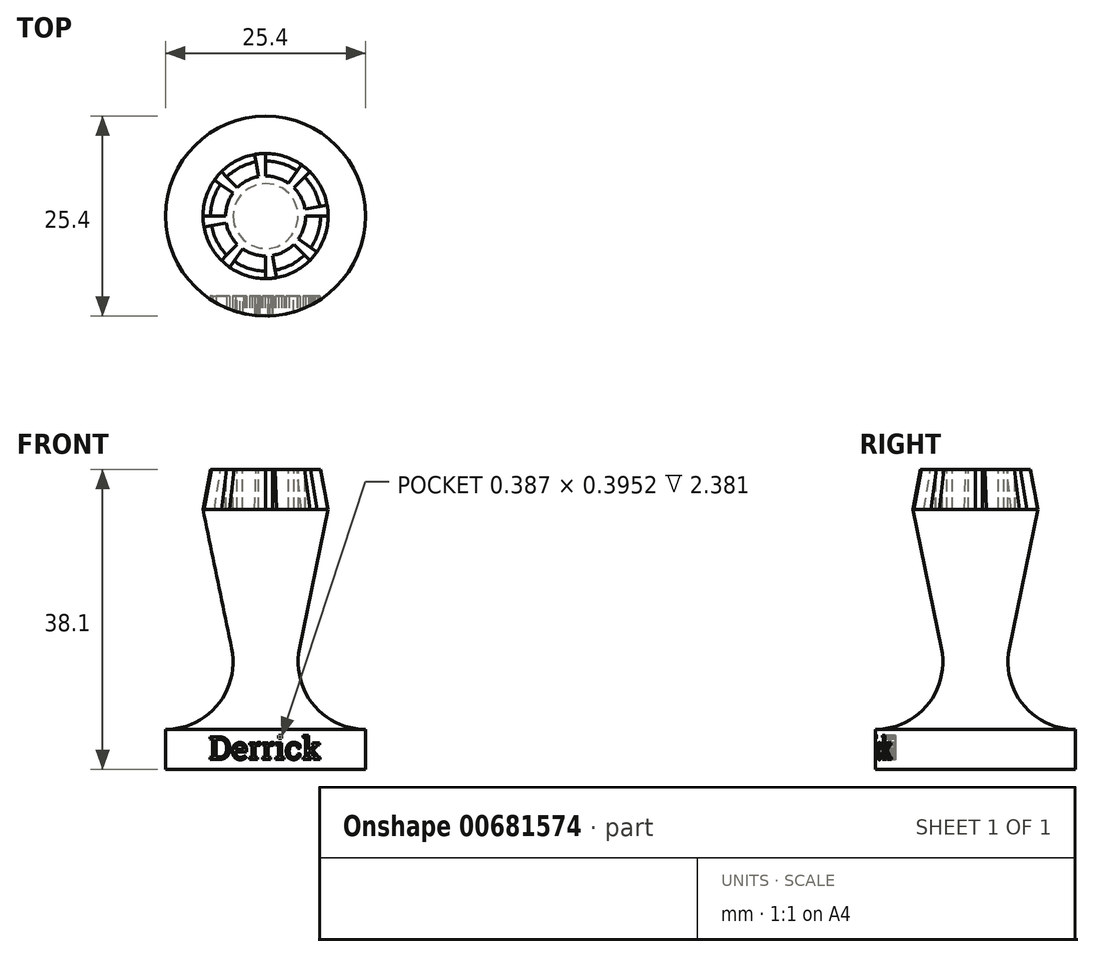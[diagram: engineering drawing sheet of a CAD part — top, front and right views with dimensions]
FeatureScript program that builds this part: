
annotation { "Feature Type Name" : "Feature", "Feature Type Description" : "" }
export const myFeature = defineFeature(function(context is Context, id is Id, definition is map)
    precondition{}
    {
        {
            var Q0;
            Q0=qCreatedBy(makeId("Front.planeOp"),FACE);
            var sketch = newSketch(context, id + "F0", { "sketchPlane" : qUnion([Q0])});
            skLineSegment(sketch, "E0", {"start": v(0, 0) * mm, "end": v(12.7, 0) * mm});
            skLineSegment(sketch, "E1", {"start": v(12.7, 0) * mm, "end": v(12.7, 5.08) * mm});
            skLineSegment(sketch, "E2", {"start": v(0, 0) * mm, "end": v(0, 38.1) * mm});
            skLineSegment(sketch, "E3", {"start": v(0, 38.1) * mm, "end": v(6.99, 38.1) * mm});
            skLineSegment(sketch, "E4", {"start": v(0, 33.02) * mm, "end": v(7.95, 33.02) * mm, "construction": true});
            skLineSegment(sketch, "E5", {"start": v(7.95, 33.02) * mm, "end": v(6.99, 38.1) * mm});
            skArc(sketch, "E6", {"start": v(4.32, 15.36) * mm, "mid": v(6.07, 8.23) * mm, "end": v(12.7, 5.08) * mm});
            skLineSegment(sketch, "E7", {"start": v(7.95, 33.02) * mm, "end": v(4.32, 15.36) * mm});
            skSolve(sketch);
        }
        {
            var Q0;
            Q0=makeQuery(id+"F0.imprint","IMPRINT",FACE,{"disambiguationData":[TD([[makeQuery(id+"F0.imprint","IMPRINT",EDGE,{"derivedFrom":sQuery(id+"F0.wireOp",EDGE,"E0")}),1.0]])]});
            var Q1;
            Q1=sQuery(id+"F0.wireOp",EDGE,"E2");
            revolve(context, id + "F1", {"entities" : qUnion([Q0]), "axis" : qUnion([Q1]), "revolveType" : RevolveType.FULL});
        }
        {
            var Q0;
            Q0=makeQuery(id+"F1.opRevolve","SWEPT_FACE",FACE,{"disambiguationData":[OSD([sQuery(id+"F0.wireOp",EDGE,"E3")])]});
            var sketch = newSketch(context, id + "F2", { "sketchPlane" : qUnion([Q0])});
            skCircle(sketch, "E8", {"center": v(0, 0) * mm, "radius": 5.08 * mm});
            skArc(sketch, "E9.0", {"start": v(-6.51, 4.56) * mm, "mid": v(-6.1, 5.11) * mm, "end": v(-5.62, 5.62) * mm});
            skLineSegment(sketch, "E10", {"start": v(0, -5.08) * mm, "end": v(0, -7.95) * mm});
            skLineSegment(sketch, "E11", {"start": v(0, -7.95) * mm, "end": v(0, -5.08) * mm});
            skLineSegment(sketch, "E12", {"start": v(0.88, -5) * mm, "end": v(1.38, -7.83) * mm});
            skLineSegment(sketch, "E13.1.2", {"start": v(4.16, -2.91) * mm, "end": v(6.51, -4.56) * mm});
            skLineSegment(sketch, "E13.1.3", {"start": v(5.62, -5.62) * mm, "end": v(3.6, -3.6) * mm});
            skLineSegment(sketch, "E13.1.4", {"start": v(3.6, -3.6) * mm, "end": v(5.62, -5.62) * mm});
            skLineSegment(sketch, "E13.2.2", {"start": v(5, 0.88) * mm, "end": v(7.83, 1.38) * mm});
            skLineSegment(sketch, "E13.2.3", {"start": v(7.95, 0) * mm, "end": v(5.08, 0) * mm});
            skLineSegment(sketch, "E13.2.4", {"start": v(5.08, 0) * mm, "end": v(7.95, 0) * mm});
            skLineSegment(sketch, "E13.3.2", {"start": v(2.91, 4.16) * mm, "end": v(4.56, 6.51) * mm});
            skLineSegment(sketch, "E13.3.3", {"start": v(5.62, 5.62) * mm, "end": v(3.6, 3.6) * mm});
            skLineSegment(sketch, "E13.3.4", {"start": v(3.6, 3.6) * mm, "end": v(5.62, 5.62) * mm});
            skLineSegment(sketch, "E13.4.2", {"start": v(-0.88, 5) * mm, "end": v(-1.38, 7.83) * mm});
            skLineSegment(sketch, "E13.4.3", {"start": v(0, 7.95) * mm, "end": v(0, 5.08) * mm});
            skLineSegment(sketch, "E13.4.4", {"start": v(0, 5.08) * mm, "end": v(0, 7.95) * mm});
            skLineSegment(sketch, "E13.5.2", {"start": v(-4.16, 2.91) * mm, "end": v(-6.51, 4.56) * mm});
            skLineSegment(sketch, "E13.5.3", {"start": v(-5.62, 5.62) * mm, "end": v(-3.6, 3.6) * mm});
            skLineSegment(sketch, "E13.5.4", {"start": v(-3.6, 3.6) * mm, "end": v(-5.62, 5.62) * mm});
            skLineSegment(sketch, "E13.6.2", {"start": v(-5, -0.88) * mm, "end": v(-7.83, -1.38) * mm});
            skLineSegment(sketch, "E13.6.3", {"start": v(-7.95, 0) * mm, "end": v(-5.08, 0) * mm});
            skLineSegment(sketch, "E13.6.4", {"start": v(-5.08, 0) * mm, "end": v(-7.95, 0) * mm});
            skLineSegment(sketch, "E13.7.2", {"start": v(-2.91, -4.16) * mm, "end": v(-4.56, -6.51) * mm});
            skLineSegment(sketch, "E13.7.3", {"start": v(-5.62, -5.62) * mm, "end": v(-3.6, -3.6) * mm});
            skLineSegment(sketch, "E13.7.4", {"start": v(-3.6, -3.6) * mm, "end": v(-5.62, -5.62) * mm});
            skArc(sketch, "E14.trimOffspring", {"start": v(-1.38, 7.83) * mm, "mid": v(-0.7, 7.92) * mm, "end": v(0, 7.95) * mm});
            skArc(sketch, "E15.trimOffspring", {"start": v(4.56, 6.51) * mm, "mid": v(5.11, 6.1) * mm, "end": v(5.62, 5.62) * mm});
            skArc(sketch, "E16.trimOffspring", {"start": v(7.83, 1.38) * mm, "mid": v(7.92, 0.7) * mm, "end": v(7.95, 0) * mm});
            skArc(sketch, "E17.trimOffspring", {"start": v(6.51, -4.56) * mm, "mid": v(6.1, -5.11) * mm, "end": v(5.62, -5.62) * mm});
            skArc(sketch, "E18.trimOffspring", {"start": v(1.38, -7.83) * mm, "mid": v(0.7, -7.92) * mm, "end": v(0, -7.95) * mm});
            skArc(sketch, "E19.trimOffspring", {"start": v(-4.56, -6.51) * mm, "mid": v(-5.11, -6.1) * mm, "end": v(-5.62, -5.62) * mm});
            skArc(sketch, "E20.trimOffspring", {"start": v(-7.83, -1.38) * mm, "mid": v(-7.92, -0.7) * mm, "end": v(-7.95, 0) * mm});
            skSolve(sketch);
        }
        {
            var Q0;
            Q0 = qSketchRegion(id + "F2", true);
            extrude(context, id + "F3", {"entities" : qUnion([Q0]), "operationType" : NewBodyOperationType.REMOVE, "oppositeDirection" : true, "depth" : 5.08 * mm, "offsetDistance" : 25.4 * mm});
        }
        {
            var Q0;
            Q0=qCreatedBy(makeId("Front.planeOp"),FACE);
            cPlane(context, id + "F4", {"entities" : qUnion([Q0]), "cplaneType" : CPlaneType.OFFSET, "offset" : 12.7 * mm, "width" : 152.4 * mm, "height" : 152.4 * mm});
        }
        {
            var Q0;
            Q0=qCreatedBy(id+"F4.planeOp",FACE);
            var sketch = newSketch(context, id + "F5", { "sketchPlane" : qUnion([Q0])});
            skText(sketch, "E21", { "text": "Derrick", "fontName": "RobotoSlab-Regular.ttf"});
            const initialGuessF5  = {"E21": [-0.00717, 0.00127, 1, 0, 0.0029]};
            skSetInitialGuess(sketch, initialGuessF5);
            skSolve(sketch);
        }
        {
            var Q0;
            Q0 = qSketchRegion(id + "F5", true);
            extrude(context, id + "F6", {"entities" : qUnion([Q0]), "operationType" : NewBodyOperationType.REMOVE, "oppositeDirection" : true, "depth" : 2.54 * mm, "offsetDistance" : 25.4 * mm});
        }
    });
